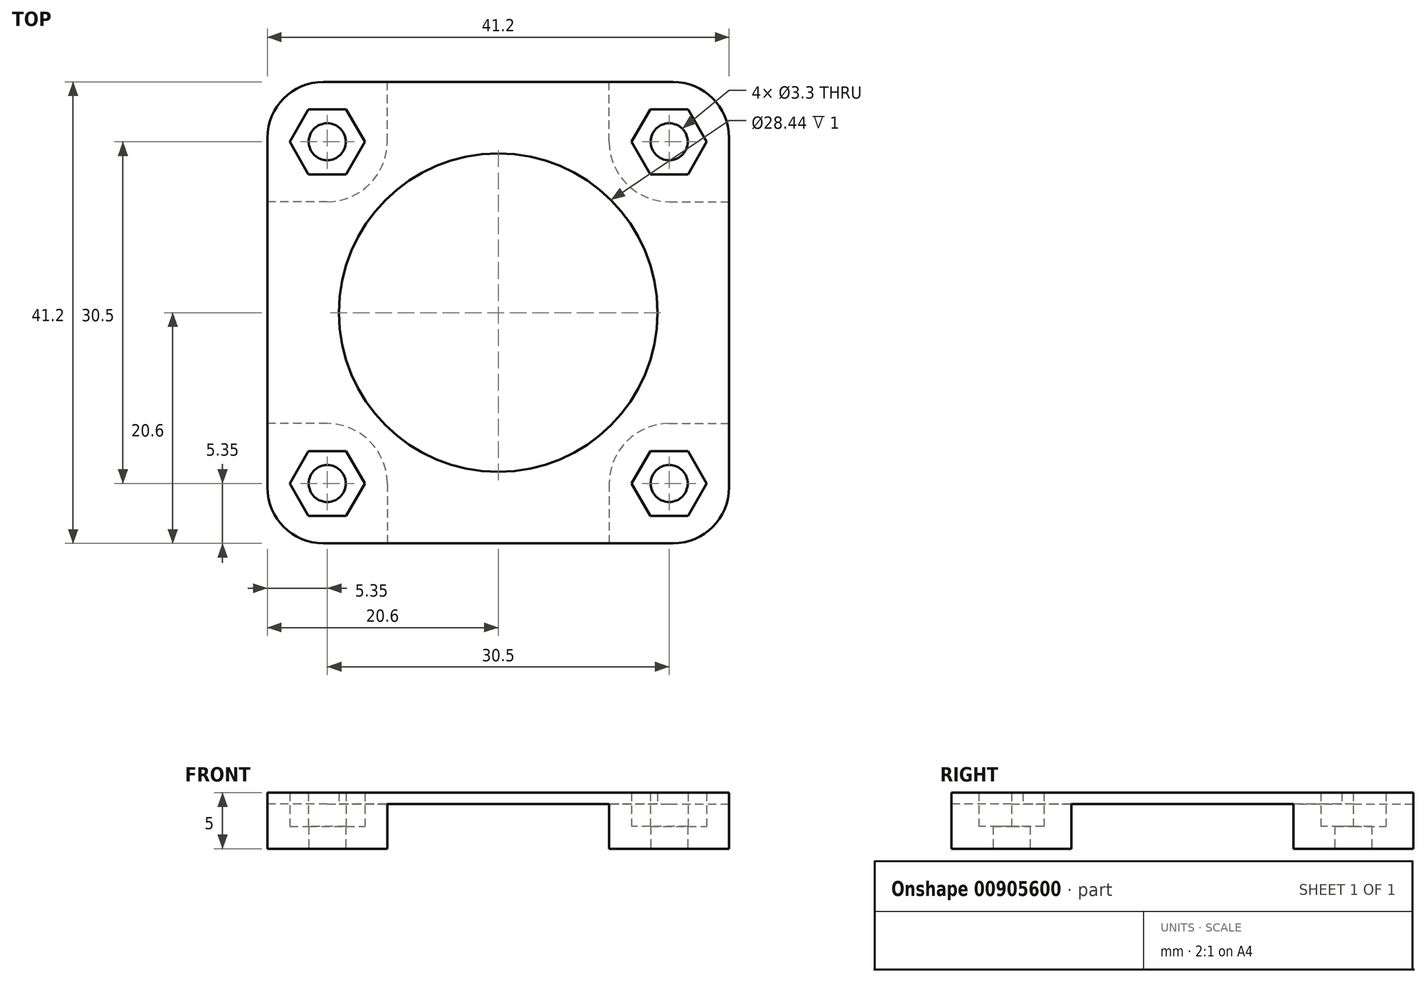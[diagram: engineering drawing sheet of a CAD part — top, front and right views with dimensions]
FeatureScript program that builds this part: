
annotation { "Feature Type Name" : "Feature", "Feature Type Description" : "" }
export const myFeature = defineFeature(function(context is Context, id is Id, definition is map)
    precondition{}
    {
        {
            var Q0;
            Q0=qCreatedBy(makeId("Top.planeOp"),FACE);
            var sketch = newSketch(context, id + "F0", { "sketchPlane" : qUnion([Q0])});
            skLineSegment(sketch, "E0.bottom", {"start": v(20.6, 20.6) * mm, "end": v(-20.6, 20.6) * mm});
            skLineSegment(sketch, "E0.top", {"start": v(20.6, -20.6) * mm, "end": v(-20.6, -20.6) * mm});
            skLineSegment(sketch, "E0.left", {"start": v(20.6, 20.6) * mm, "end": v(20.6, -20.6) * mm});
            skLineSegment(sketch, "E0.right", {"start": v(-20.6, 20.6) * mm, "end": v(-20.6, -20.6) * mm});
            skPoint(sketch, "E0.middle", {"position": v(0, 0) * mm});
            skLineSegment(sketch, "E1.bottom", {"start": v(15.25, 15.25) * mm, "end": v(-15.25, 15.25) * mm, "construction": true});
            skLineSegment(sketch, "E1.top", {"start": v(15.25, -15.25) * mm, "end": v(-15.25, -15.25) * mm, "construction": true});
            skLineSegment(sketch, "E1.left", {"start": v(15.25, 15.25) * mm, "end": v(15.25, -15.25) * mm, "construction": true});
            skLineSegment(sketch, "E1.right", {"start": v(-15.25, 15.25) * mm, "end": v(-15.25, -15.25) * mm, "construction": true});
            skCircle(sketch, "E2", {"center": v(-15.25, 15.25) * mm, "radius": 1.65 * mm});
            skCircle(sketch, "E3", {"center": v(15.25, 15.25) * mm, "radius": 1.65 * mm});
            skCircle(sketch, "E4", {"center": v(15.25, -15.25) * mm, "radius": 1.65 * mm});
            skCircle(sketch, "E5", {"center": v(-15.25, -15.25) * mm, "radius": 1.65 * mm});
            skCircle(sketch, "E6.cCircle", {"center": v(-15.25, 15.25) * mm, "radius": 2.9 * mm, "construction": true});
            skLineSegment(sketch, "E6.0", {"start": v(-16.92, 18.15) * mm, "end": v(-13.58, 18.15) * mm});
            skLineSegment(sketch, "E6.1", {"start": v(-13.58, 18.15) * mm, "end": v(-11.9, 15.25) * mm});
            skLineSegment(sketch, "E6.2", {"start": v(-11.9, 15.25) * mm, "end": v(-13.58, 12.35) * mm});
            skLineSegment(sketch, "E6.3", {"start": v(-13.58, 12.35) * mm, "end": v(-16.92, 12.35) * mm});
            skLineSegment(sketch, "E6.4", {"start": v(-16.92, 12.35) * mm, "end": v(-18.6, 15.25) * mm});
            skLineSegment(sketch, "E6.5", {"start": v(-18.6, 15.25) * mm, "end": v(-16.92, 18.15) * mm});
            skPoint(sketch, "E6.0.midPoint", {"position": v(-15.25, 18.15) * mm});
            skCircle(sketch, "E7.cCircle", {"center": v(15.25, 15.25) * mm, "radius": 2.9 * mm, "construction": true});
            skLineSegment(sketch, "E7.0", {"start": v(16.92, 18.15) * mm, "end": v(18.6, 15.25) * mm});
            skLineSegment(sketch, "E7.1", {"start": v(18.6, 15.25) * mm, "end": v(16.92, 12.35) * mm});
            skLineSegment(sketch, "E7.2", {"start": v(16.92, 12.35) * mm, "end": v(13.58, 12.35) * mm});
            skLineSegment(sketch, "E7.3", {"start": v(13.58, 12.35) * mm, "end": v(11.9, 15.25) * mm});
            skLineSegment(sketch, "E7.4", {"start": v(11.9, 15.25) * mm, "end": v(13.58, 18.15) * mm});
            skLineSegment(sketch, "E7.5", {"start": v(13.58, 18.15) * mm, "end": v(16.92, 18.15) * mm});
            skPoint(sketch, "E7.0.midPoint", {"position": v(17.76, 16.7) * mm});
            skCircle(sketch, "E8.cCircle", {"center": v(15.25, -15.25) * mm, "radius": 2.9 * mm, "construction": true});
            skLineSegment(sketch, "E8.0", {"start": v(16.92, -12.35) * mm, "end": v(18.6, -15.25) * mm});
            skLineSegment(sketch, "E8.1", {"start": v(18.6, -15.25) * mm, "end": v(16.92, -18.15) * mm});
            skLineSegment(sketch, "E8.2", {"start": v(16.92, -18.15) * mm, "end": v(13.58, -18.15) * mm});
            skLineSegment(sketch, "E8.3", {"start": v(13.58, -18.15) * mm, "end": v(11.9, -15.25) * mm});
            skLineSegment(sketch, "E8.4", {"start": v(11.9, -15.25) * mm, "end": v(13.58, -12.35) * mm});
            skLineSegment(sketch, "E8.5", {"start": v(13.58, -12.35) * mm, "end": v(16.92, -12.35) * mm});
            skPoint(sketch, "E8.0.midPoint", {"position": v(17.76, -13.8) * mm});
            skCircle(sketch, "E9.cCircle", {"center": v(-15.25, -15.25) * mm, "radius": 2.9 * mm, "construction": true});
            skLineSegment(sketch, "E9.0", {"start": v(-13.58, -12.35) * mm, "end": v(-11.9, -15.25) * mm});
            skLineSegment(sketch, "E9.1", {"start": v(-11.9, -15.25) * mm, "end": v(-13.58, -18.15) * mm});
            skLineSegment(sketch, "E9.2", {"start": v(-13.58, -18.15) * mm, "end": v(-16.92, -18.15) * mm});
            skLineSegment(sketch, "E9.3", {"start": v(-16.92, -18.15) * mm, "end": v(-18.6, -15.25) * mm});
            skLineSegment(sketch, "E9.4", {"start": v(-18.6, -15.25) * mm, "end": v(-16.92, -12.35) * mm});
            skLineSegment(sketch, "E9.5", {"start": v(-16.92, -12.35) * mm, "end": v(-13.58, -12.35) * mm});
            skPoint(sketch, "E9.0.midPoint", {"position": v(-12.74, -13.8) * mm});
            skSolve(sketch);
        }
        {
            var Q0;
            Q0=makeQuery(id+"F0.imprint","IMPRINT",FACE,{"disambiguationData":[TD([[makeQuery(id+"F0.imprint","IMPRINT",EDGE,{"derivedFrom":sQuery(id+"F0.wireOp",EDGE,"E0.bottom")}),1.0]])]});
            extrude(context, id + "F1", {"entities" : qUnion([Q0]), "depth" : 5 * mm, "offsetDistance" : 25 * mm});
        }
        {
            var Q0;
            Q0=makeQuery(id+"F0.imprint","IMPRINT",FACE,{"disambiguationData":[TD([[makeQuery(id+"F0.imprint","IMPRINT",EDGE,{"derivedFrom":sQuery(id+"F0.wireOp",EDGE,"E2")}),-1.0]])]});
            var Q1;
            Q1=makeQuery(id+"F0.imprint","IMPRINT",FACE,{"disambiguationData":[TD([[makeQuery(id+"F0.imprint","IMPRINT",EDGE,{"derivedFrom":sQuery(id+"F0.wireOp",EDGE,"E3")}),-1.0]])]});
            var Q2;
            Q2=makeQuery(id+"F0.imprint","IMPRINT",FACE,{"disambiguationData":[TD([[makeQuery(id+"F0.imprint","IMPRINT",EDGE,{"derivedFrom":sQuery(id+"F0.wireOp",EDGE,"E4")}),-1.0]])]});
            var Q3;
            Q3=makeQuery(id+"F0.imprint","IMPRINT",FACE,{"disambiguationData":[TD([[makeQuery(id+"F0.imprint","IMPRINT",EDGE,{"derivedFrom":sQuery(id+"F0.wireOp",EDGE,"E5")}),-1.0]])]});
            extrude(context, id + "F2", {"entities" : qUnion([Q0, Q1, Q2, Q3]), "operationType" : NewBodyOperationType.ADD, "depth" : 2 * mm, "offsetDistance" : 25 * mm});
        }
        {
            var Q0;
            {var subQ0=sQuery(id+"F0.wireOp",EDGE,"E9.5");var subQ1=sQuery(id+"F0.wireOp",EDGE,"E9.4");var subQ2=sQuery(id+"F0.wireOp",EDGE,"E9.3");var subQ3=sQuery(id+"F0.wireOp",EDGE,"E9.2");var subQ4=sQuery(id+"F0.wireOp",EDGE,"E9.1");var subQ5=sQuery(id+"F0.wireOp",EDGE,"E9.0");var subQ6=sQuery(id+"F0.wireOp",EDGE,"E8.5");var subQ7=sQuery(id+"F0.wireOp",EDGE,"E8.4");var subQ8=sQuery(id+"F0.wireOp",EDGE,"E8.3");var subQ9=sQuery(id+"F0.wireOp",EDGE,"E8.2");var subQ10=sQuery(id+"F0.wireOp",EDGE,"E8.1");var subQ11=sQuery(id+"F0.wireOp",EDGE,"E8.0");var subQ12=sQuery(id+"F0.wireOp",EDGE,"E7.5");var subQ13=sQuery(id+"F0.wireOp",EDGE,"E7.4");var subQ14=sQuery(id+"F0.wireOp",EDGE,"E7.3");var subQ15=sQuery(id+"F0.wireOp",EDGE,"E7.2");var subQ16=sQuery(id+"F0.wireOp",EDGE,"E7.1");var subQ17=sQuery(id+"F0.wireOp",EDGE,"E7.0");var subQ18=sQuery(id+"F0.wireOp",EDGE,"E6.5");var subQ19=sQuery(id+"F0.wireOp",EDGE,"E6.4");var subQ20=sQuery(id+"F0.wireOp",EDGE,"E6.3");var subQ21=sQuery(id+"F0.wireOp",EDGE,"E6.2");var subQ22=sQuery(id+"F0.wireOp",EDGE,"E6.1");var subQ23=sQuery(id+"F0.wireOp",EDGE,"E6.0");Q0=makeQuery(id+"F2.boolean.opBoolean","MERGE",FACE,{"derivedFrom":[makeQuery(id+"F1.opExtrude","CAP_FACE",FACE,{"disambiguationData":[OSD([sQuery(id+"F0.wireOp",EDGE,"E0.bottom"),sQuery(id+"F0.wireOp",EDGE,"E0.top"),sQuery(id+"F0.wireOp",EDGE,"E0.left"),sQuery(id+"F0.wireOp",EDGE,"E0.right"),subQ23,subQ22,subQ21,subQ20,subQ19,subQ18,subQ17,subQ16,subQ15,subQ14,subQ13,subQ12,subQ11,subQ10,subQ9,subQ8,subQ7,subQ6,subQ5,subQ4,subQ3,subQ2,subQ1,subQ0])],"isStart":true}),makeQuery(id+"F2.opExtrude","CAP_FACE",FACE,{"disambiguationData":[OSD([sQuery(id+"F0.wireOp",EDGE,"E2"),subQ23,subQ22,subQ21,subQ20,subQ19,subQ18])],"isStart":true}),makeQuery(id+"F2.opExtrude","CAP_FACE",FACE,{"disambiguationData":[OSD([sQuery(id+"F0.wireOp",EDGE,"E3"),subQ17,subQ16,subQ15,subQ14,subQ13,subQ12])],"isStart":true}),makeQuery(id+"F2.opExtrude","CAP_FACE",FACE,{"disambiguationData":[OSD([sQuery(id+"F0.wireOp",EDGE,"E4"),subQ11,subQ10,subQ9,subQ8,subQ7,subQ6])],"isStart":true}),makeQuery(id+"F2.opExtrude","CAP_FACE",FACE,{"disambiguationData":[OSD([sQuery(id+"F0.wireOp",EDGE,"E5"),subQ5,subQ4,subQ3,subQ2,subQ1,subQ0])],"isStart":true})]});}
            var sketch = newSketch(context, id + "F3", { "sketchPlane" : qUnion([Q0])});
            skCircle(sketch, "E10.0", {"center": v(-15.25, 15.25) * mm, "radius": 1.65 * mm, "construction": true});
            skCircle(sketch, "E11.0", {"center": v(15.25, 15.25) * mm, "radius": 1.65 * mm, "construction": true});
            skCircle(sketch, "E12.0", {"center": v(15.25, -15.25) * mm, "radius": 1.65 * mm, "construction": true});
            skCircle(sketch, "E13.0", {"center": v(-15.25, -15.25) * mm, "radius": 1.65 * mm, "construction": true});
            skLineSegment(sketch, "E14.0", {"start": v(-20.6, -9.9) * mm, "end": v(-20.6, 9.9) * mm});
            skLineSegment(sketch, "E15.0", {"start": v(9.9, 20.6) * mm, "end": v(-9.9, 20.6) * mm});
            skLineSegment(sketch, "E16.0", {"start": v(20.6, -9.9) * mm, "end": v(20.6, 9.9) * mm});
            skLineSegment(sketch, "E17.0", {"start": v(9.9, -20.6) * mm, "end": v(-9.9, -20.6) * mm});
            skArc(sketch, "E18", {"start": v(-9.9, 15.25) * mm, "mid": v(-11.47, 11.47) * mm, "end": v(-15.25, 9.9) * mm});
            skArc(sketch, "E19", {"start": v(-15.25, -9.9) * mm, "mid": v(-11.47, -11.47) * mm, "end": v(-9.9, -15.25) * mm});
            skArc(sketch, "E20", {"start": v(15.25, -9.9) * mm, "mid": v(11.47, -11.47) * mm, "end": v(9.9, -15.25) * mm});
            skArc(sketch, "E21", {"start": v(15.25, 9.9) * mm, "mid": v(11.47, 11.47) * mm, "end": v(9.9, 15.25) * mm});
            skLineSegment(sketch, "E22", {"start": v(15.25, 9.9) * mm, "end": v(20.6, 9.9) * mm});
            skLineSegment(sketch, "E23", {"start": v(9.9, 15.25) * mm, "end": v(9.9, 20.6) * mm});
            skLineSegment(sketch, "E24", {"start": v(15.25, -9.9) * mm, "end": v(20.6, -9.9) * mm});
            skLineSegment(sketch, "E25", {"start": v(9.9, -15.25) * mm, "end": v(9.9, -20.6) * mm});
            skLineSegment(sketch, "E26", {"start": v(-9.9, -15.25) * mm, "end": v(-9.9, -20.6) * mm});
            skLineSegment(sketch, "E27", {"start": v(-15.25, -9.9) * mm, "end": v(-20.6, -9.9) * mm});
            skLineSegment(sketch, "E28", {"start": v(-15.25, 9.9) * mm, "end": v(-20.6, 9.9) * mm});
            skLineSegment(sketch, "E29", {"start": v(-9.9, 15.25) * mm, "end": v(-9.9, 20.6) * mm});
            skLineSegment(sketch, "E30.0", {"start": v(-13.58, 12.35) * mm, "end": v(-11.9, 15.25) * mm, "construction": true});
            skLineSegment(sketch, "E31.0", {"start": v(-11.9, -15.25) * mm, "end": v(-13.58, -12.35) * mm, "construction": true});
            skLineSegment(sketch, "E32.0", {"start": v(11.9, 15.25) * mm, "end": v(13.58, 12.35) * mm, "construction": true});
            skLineSegment(sketch, "E33.0", {"start": v(13.58, -12.35) * mm, "end": v(11.9, -15.25) * mm, "construction": true});
            skPoint(sketch, "E34.orphan", {"position": v(-20.6, 20.6) * mm});
            skPoint(sketch, "E35.orphan", {"position": v(-20.6, -20.6) * mm});
            skPoint(sketch, "E36.orphan", {"position": v(20.6, -20.6) * mm});
            skPoint(sketch, "E37.orphan", {"position": v(20.6, 20.6) * mm});
            skSolve(sketch);
        }
        {
            var Q0;
            Q0 = qSketchRegion(id + "F3", true);
            extrude(context, id + "F4", {"entities" : qUnion([Q0]), "operationType" : NewBodyOperationType.REMOVE, "oppositeDirection" : true, "depth" : 4 * mm, "offsetDistance" : 25 * mm});
        }
        {
            var Q0;
            Q0=makeQuery(id+"F4.boolean.opBoolean","COPY",FACE,{"derivedFrom":makeQuery(id+"F4.opExtrude","CAP_FACE",FACE,{"disambiguationData":[OSD([sQuery(id+"F3.wireOp",EDGE,"E14.0"),sQuery(id+"F3.wireOp",EDGE,"E15.0"),sQuery(id+"F3.wireOp",EDGE,"E16.0"),sQuery(id+"F3.wireOp",EDGE,"E17.0"),sQuery(id+"F3.wireOp",EDGE,"E18"),sQuery(id+"F3.wireOp",EDGE,"E19"),sQuery(id+"F3.wireOp",EDGE,"E20"),sQuery(id+"F3.wireOp",EDGE,"E21"),sQuery(id+"F3.wireOp",EDGE,"E22"),sQuery(id+"F3.wireOp",EDGE,"E23"),sQuery(id+"F3.wireOp",EDGE,"E24"),sQuery(id+"F3.wireOp",EDGE,"E25"),sQuery(id+"F3.wireOp",EDGE,"E26"),sQuery(id+"F3.wireOp",EDGE,"E27"),sQuery(id+"F3.wireOp",EDGE,"E28"),sQuery(id+"F3.wireOp",EDGE,"E29")])],"isStart":false})});
            var sketch = newSketch(context, id + "F5", { "sketchPlane" : qUnion([Q0])});
            skCircle(sketch, "E38", {"center": v(0, 0) * mm, "radius": 14.22 * mm});
            skArc(sketch, "E39.0", {"start": v(15.25, 9.9) * mm, "mid": v(11.47, 11.47) * mm, "end": v(9.9, 15.25) * mm, "construction": true});
            skSolve(sketch);
        }
        {
            var Q0;
            Q0 = qSketchRegion(id + "F5", true);
            extrude(context, id + "F6", {"entities" : qUnion([Q0]), "operationType" : NewBodyOperationType.REMOVE, "endBound" : BoundingType.THROUGH_ALL, "oppositeDirection" : true, "depth" : 25 * mm, "offsetDistance" : 25 * mm});
        }
        {
            var Q0;
            Q0=makeQuery(id+"F1.opExtrude","SWEPT_EDGE",EDGE,{"disambiguationData":[OSD([sQuery(id+"F0.wireOp",EDGE,"E0.bottom"),sQuery(id+"F0.wireOp",EDGE,"E0.right")])]});
            var Q1;
            Q1=makeQuery(id+"F1.opExtrude","SWEPT_EDGE",EDGE,{"disambiguationData":[OSD([sQuery(id+"F0.wireOp",EDGE,"E0.bottom"),sQuery(id+"F0.wireOp",EDGE,"E0.left")])]});
            var Q2;
            Q2=makeQuery(id+"F1.opExtrude","SWEPT_EDGE",EDGE,{"disambiguationData":[OSD([sQuery(id+"F0.wireOp",EDGE,"E0.top"),sQuery(id+"F0.wireOp",EDGE,"E0.left")])]});
            var Q3;
            Q3=makeQuery(id+"F1.opExtrude","SWEPT_EDGE",EDGE,{"disambiguationData":[OSD([sQuery(id+"F0.wireOp",EDGE,"E0.top"),sQuery(id+"F0.wireOp",EDGE,"E0.right")])]});
            var Q4;
            Q4=makeQuery(id+"F4.boolean.opBoolean","COPY",EDGE,{"derivedFrom":makeQuery(id+"F4.opExtrude","SWEPT_EDGE",EDGE,{"disambiguationData":[OSD([sQuery(id+"F0.wireOp",EDGE,"E0.right"),sQuery(id+"F3.wireOp",EDGE,"E14.0"),sQuery(id+"F3.wireOp",EDGE,"E28")])]})});
            var Q5;
            Q5=makeQuery(id+"F4.boolean.opBoolean","COPY",EDGE,{"derivedFrom":makeQuery(id+"F4.opExtrude","SWEPT_EDGE",EDGE,{"disambiguationData":[OSD([sQuery(id+"F0.wireOp",EDGE,"E0.top"),sQuery(id+"F3.wireOp",EDGE,"E15.0"),sQuery(id+"F3.wireOp",EDGE,"E29")])]})});
            var Q6;
            Q6=makeQuery(id+"F4.boolean.opBoolean","COPY",EDGE,{"derivedFrom":makeQuery(id+"F4.opExtrude","SWEPT_EDGE",EDGE,{"disambiguationData":[OSD([sQuery(id+"F0.wireOp",EDGE,"E0.right"),sQuery(id+"F3.wireOp",EDGE,"E14.0"),sQuery(id+"F3.wireOp",EDGE,"E27")])]})});
            var Q7;
            Q7=makeQuery(id+"F4.boolean.opBoolean","COPY",EDGE,{"derivedFrom":makeQuery(id+"F4.opExtrude","SWEPT_EDGE",EDGE,{"disambiguationData":[OSD([sQuery(id+"F0.wireOp",EDGE,"E0.bottom"),sQuery(id+"F3.wireOp",EDGE,"E17.0"),sQuery(id+"F3.wireOp",EDGE,"E26")])]})});
            var Q8;
            Q8=makeQuery(id+"F4.boolean.opBoolean","COPY",EDGE,{"derivedFrom":makeQuery(id+"F4.opExtrude","SWEPT_EDGE",EDGE,{"disambiguationData":[OSD([sQuery(id+"F0.wireOp",EDGE,"E0.bottom"),sQuery(id+"F3.wireOp",EDGE,"E17.0"),sQuery(id+"F3.wireOp",EDGE,"E25")])]})});
            var Q9;
            Q9=makeQuery(id+"F4.boolean.opBoolean","COPY",EDGE,{"derivedFrom":makeQuery(id+"F4.opExtrude","SWEPT_EDGE",EDGE,{"disambiguationData":[OSD([sQuery(id+"F0.wireOp",EDGE,"E0.left"),sQuery(id+"F3.wireOp",EDGE,"E16.0"),sQuery(id+"F3.wireOp",EDGE,"E24")])]})});
            var Q10;
            Q10=makeQuery(id+"F4.boolean.opBoolean","COPY",EDGE,{"derivedFrom":makeQuery(id+"F4.opExtrude","SWEPT_EDGE",EDGE,{"disambiguationData":[OSD([sQuery(id+"F0.wireOp",EDGE,"E0.left"),sQuery(id+"F3.wireOp",EDGE,"E16.0"),sQuery(id+"F3.wireOp",EDGE,"E22")])]})});
            var Q11;
            Q11=makeQuery(id+"F4.boolean.opBoolean","COPY",EDGE,{"derivedFrom":makeQuery(id+"F4.opExtrude","SWEPT_EDGE",EDGE,{"disambiguationData":[OSD([sQuery(id+"F0.wireOp",EDGE,"E0.top"),sQuery(id+"F3.wireOp",EDGE,"E15.0"),sQuery(id+"F3.wireOp",EDGE,"E23")])]})});
            fillet(context, id + "F7", {"entities" : qUnion([Q0, Q1, Q2, Q3, Q4, Q5, Q6, Q7, Q8, Q9, Q10, Q11]), "radius" : 5 * mm, "tangentPropagation" : true, "allowEdgeOverflow" : false});
        }
    });
